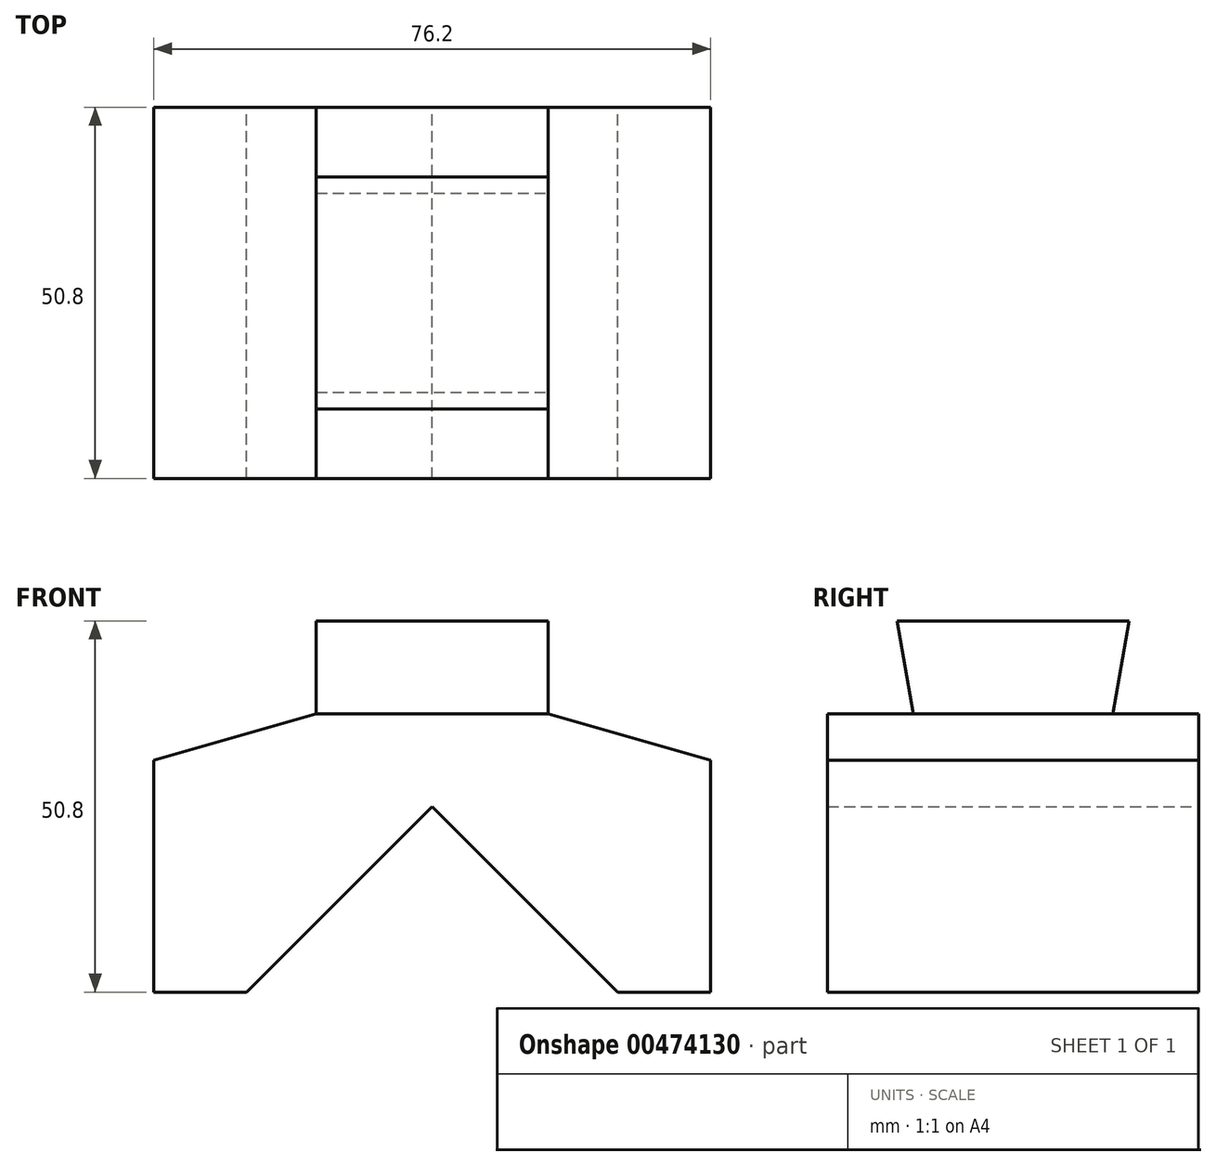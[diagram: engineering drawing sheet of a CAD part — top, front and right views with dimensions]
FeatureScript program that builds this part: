
annotation { "Feature Type Name" : "Feature", "Feature Type Description" : "" }
export const myFeature = defineFeature(function(context is Context, id is Id, definition is map)
    precondition{}
    {
        {
            var Q0;
            Q0=qCreatedBy(makeId("Front.planeOp"),FACE);
            var sketch = newSketch(context, id + "F0", { "sketchPlane" : qUnion([Q0])});
            skLineSegment(sketch, "E0.bottom", {"start": v(-15.88, 6.35) * mm, "end": v(15.88, 6.35) * mm});
            skLineSegment(sketch, "E0.top", {"start": v(-15.88, -6.35) * mm, "end": v(15.88, -6.35) * mm});
            skLineSegment(sketch, "E0.left", {"start": v(-15.88, 6.35) * mm, "end": v(-15.88, -6.35) * mm});
            skLineSegment(sketch, "E0.right", {"start": v(15.88, 6.35) * mm, "end": v(15.88, -6.35) * mm});
            skPoint(sketch, "E0.middle", {"position": v(0, 0) * mm});
            skLineSegment(sketch, "E1.bottom", {"start": v(15.88, -6.35) * mm, "end": v(-15.88, -6.35) * mm});
            skLineSegment(sketch, "E1.top", {"start": v(38.1, -44.45) * mm, "end": v(25.4, -44.45) * mm});
            skLineSegment(sketch, "E1.left", {"start": v(38.1, -12.7) * mm, "end": v(38.1, -44.45) * mm});
            skLineSegment(sketch, "E1.right", {"start": v(-38.1, -12.7) * mm, "end": v(-38.1, -44.45) * mm});
            skLineSegment(sketch, "E2", {"start": v(15.88, -6.35) * mm, "end": v(38.1, -12.7) * mm});
            skLineSegment(sketch, "E3", {"start": v(-15.88, -6.35) * mm, "end": v(-38.1, -12.7) * mm});
            skPoint(sketch, "E4.orphan", {"position": v(38.1, -6.35) * mm});
            skPoint(sketch, "E5", {"position": v(0, -19.05) * mm});
            skLineSegment(sketch, "E6", {"start": v(0, -19.05) * mm, "end": v(25.4, -44.45) * mm});
            skLineSegment(sketch, "E7", {"start": v(0, -19.05) * mm, "end": v(-25.4, -44.45) * mm});
            skLineSegment(sketch, "E8.trimOffspring", {"start": v(-25.4, -44.45) * mm, "end": v(-38.1, -44.45) * mm});
            skSolve(sketch);
        }
        {
            var Q0;
            Q0 = qSketchRegion(id + "F0", true);
            extrude(context, id + "F1", {"entities" : qUnion([Q0]), "endBound" : BoundingType.SYMMETRIC, "depth" : 50.8 * mm});
        }
        {
            var Q0;
            Q0=makeQuery(id+"F1.opExtrude","SWEPT_FACE",FACE,{"disambiguationData":[OSD([sQuery(id+"F0.wireOp",EDGE,"E0.right")])]});
            var sketch = newSketch(context, id + "F2", { "sketchPlane" : qUnion([Q0])});
            skLineSegment(sketch, "E9", {"start": v(-15.88, 6.35) * mm, "end": v(-13.64, -6.35) * mm});
            skLineSegment(sketch, "E10", {"start": v(15.88, 6.35) * mm, "end": v(13.64, -6.35) * mm});
            skSolve(sketch);
        }
        {
            var Q0;
            {var subQ0=sQuery(id+"F2.wireOp",EDGE,"E9");Q0=makeQuery(id+"F2.imprint","IMPRINT",FACE,{"disambiguationData":[TD([[makeQuery(id+"F2.imprint","IMPRINT",EDGE,{"derivedFrom":subQ0}),-1.0]])]});}
            var Q1;
            {var subQ0=sQuery(id+"F2.wireOp",EDGE,"E10");Q1=makeQuery(id+"F2.imprint","IMPRINT",FACE,{"disambiguationData":[TD([[makeQuery(id+"F2.imprint","IMPRINT",EDGE,{"derivedFrom":subQ0}),1.0]])]});}
            extrude(context, id + "F3", {"entities" : qUnion([Q0, Q1]), "operationType" : NewBodyOperationType.REMOVE, "endBound" : BoundingType.THROUGH_ALL, "oppositeDirection" : true, "depth" : 25.4 * mm});
        }
    });
